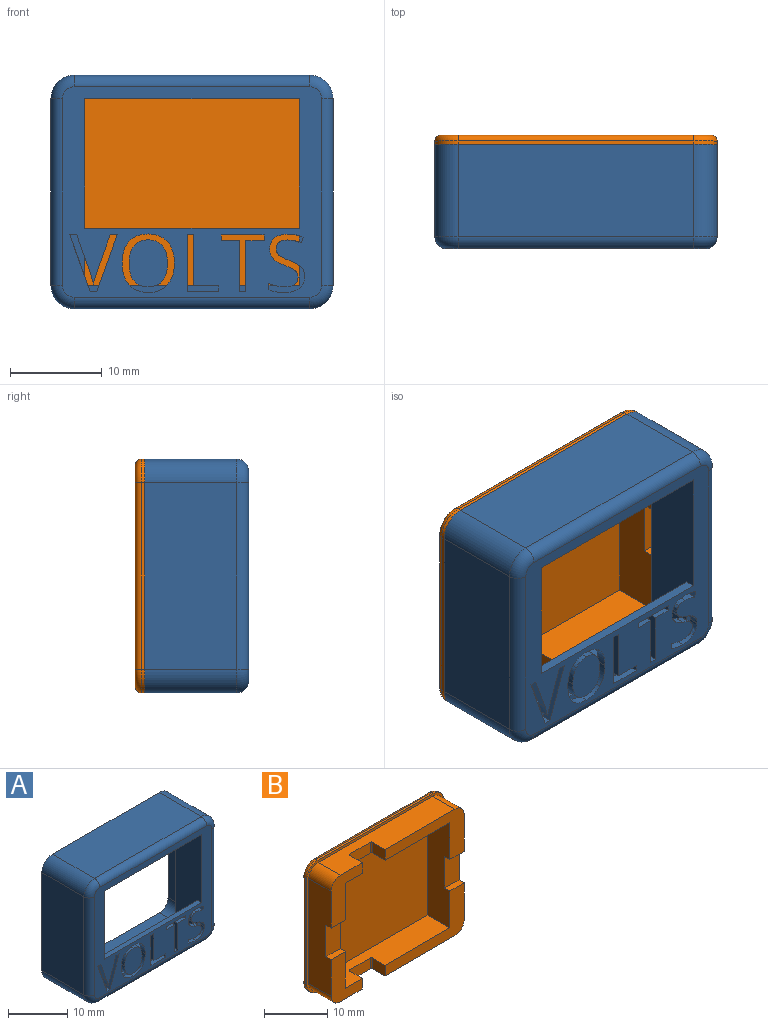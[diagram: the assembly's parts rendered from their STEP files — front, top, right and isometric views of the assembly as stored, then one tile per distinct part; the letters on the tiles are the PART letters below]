
ASSEMBLY  parts=2 mates=1
PART A: 113 faces, bbox 31.1x11.3x25.8 mm
  f0: plane 1.03x0.37mm, normal (0,1,0), area 0.2mm2, adj f7,f18,f90
  f1: plane 23.39x6.23mm, normal (0,1,0), area 91mm2, adj f6,f7,f17,f18,f29,f30,f31,f32
  f2: plane 2.81x2.55mm, normal (0,1,0), area 5.1mm2, adj f17,f64,f65,f66,f67,f68,f69,f70
  f3: plane 4.98x4.17mm, normal (0,1,0), area 17.4mm2, adj f18,f36,f37,f38,f39,f40,f41,f42
  f4: plane 28.13x22.86mm, normal (0,-1,0), area 251.7mm2, adj f6,f7,f8,f17,f29,f30,f31,f32
  f5: plane 29.72x24.92mm, normal (0,1,0), area 250.5mm2, adj f7,f8,f9,f17,f18,f19,f20,f21
  f6: plane 23.37x1.02mm, normal (0,0,1), area 23.7mm2, adj f1,f4,f7,f17
  f7: plane 20.32x6.35mm, normal (1,0,0), area 122.7mm2, adj f0,f1,f4,f5,f6,f8,f18,f99
  f8: plane 23.37x6.35mm, normal (0,0,-1), area 148.4mm2, adj f4,f5,f7,f17
  f9: plane 25.59x10.03mm, normal (0,0,-1), area 241.3mm2, adj f5,f10,f16,f27,f107,f108,f109,f110
  f10: cylinder r=2.54mm len=10.03mm, axis (0,-1,0), area 40mm2, adj f9,f11,f27,f105
  f11: plane 20.32x10.03mm, normal (1,0,0), area 203.9mm2, adj f10,f12,f27,f103
  f12: cylinder r=2.54mm len=10.03mm, axis (0,-1,0), area 40mm2, adj f11,f13,f27,f101
  f13: plane 25.59x10.03mm, normal (0,0,1), area 256.7mm2, adj f12,f14,f27,f100
  f14: cylinder r=2.54mm len=10.03mm, axis (0,-1,0), area 40mm2, adj f13,f15,f27,f102
  f15: plane 20.32x10.03mm, normal (-1,0,0), area 203.9mm2, adj f14,f16,f27,f104
  f16: cylinder r=2.54mm len=10.03mm, axis (0,-1,0), area 40mm2, adj f9,f15,f27,f106
  f17: plane 20.32x6.35mm, normal (-1,0,0), area 122.7mm2, adj f1,f2,f4,f5,f6,f8,f18,f53
  f18: plane 23.37x5.33mm, normal (0,0,1), area 124.6mm2, adj f0,f1,f3,f5,f7,f17,f28,f46
  f19: plane 25.59x4.95mm, normal (0,0,1), area 111.3mm2, adj f5,f20,f26,f27,f108,f109,f110,f111
  f20: cylinder r=2.06mm len=4.95mm, axis (0,-1,0), area 16.1mm2, adj f5,f19,f21,f27
  f21: plane 20.32x4.95mm, normal (1,0,0), area 100.6mm2, adj f5,f20,f22,f27
  f22: cylinder r=2.06mm len=4.95mm, axis (0,-1,0), area 16.1mm2, adj f5,f21,f23,f27
  f23: plane 25.59x4.95mm, normal (0,0,-1), area 126.7mm2, adj f5,f22,f24,f27
  f24: cylinder r=2.06mm len=4.95mm, axis (0,-1,0), area 16.1mm2, adj f5,f23,f25,f27
  f25: plane 20.32x4.95mm, normal (-1,0,0), area 100.6mm2, adj f5,f24,f26,f27
  f26: cylinder r=2.06mm len=4.95mm, axis (0,-1,0), area 16.1mm2, adj f5,f19,f25,f27
  f27: plane 30.67x25.4mm, normal (0,1,0), area 50.6mm2, adj f9,f10,f11,f12,f13,f14,f15,f16
  f28: plane 4.2x0.85mm, normal (0,-1,0), area 2.1mm2, adj f18,f29,f30,f36,f37
  f29: extruded ~2.11x1.02mm, area 2.4mm2, adj f1,f4,f28,f30,f44
  f30: extruded ~2.09x1.02mm, area 2.4mm2, adj f1,f4,f28,f29,f31
  f31: extruded ~2.34x1.02mm, area 2.5mm2, adj f1,f4,f30,f32
  f32: extruded ~2.34x1.02mm, area 2.5mm2, adj f1,f4,f31,f33
  f33: extruded ~2.08x1.02mm, area 2.4mm2, adj f1,f4,f32,f34
  f34: extruded ~2.12x1.02mm, area 2.4mm2, adj f1,f4,f33,f35
  f35: extruded ~2.34x1.02mm, area 2.6mm2, adj f1,f4,f34,f44
  f36: extruded ~1.55x1.02mm, area 1.8mm2, adj f3,f28,f37,f43,f45
  f37: extruded ~1.56x1.02mm, area 1.8mm2, adj f3,f28,f36,f38,f45
  f38: extruded ~1.91x1.02mm, area 2.1mm2, adj f3,f37,f39,f45
  f39: extruded ~1.89x1.02mm, area 2mm2, adj f3,f38,f40,f45
  f40: extruded ~1.56x1.02mm, area 1.8mm2, adj f3,f39,f41,f45
  f41: extruded ~1.55x1.02mm, area 1.8mm2, adj f3,f40,f42,f45
  f42: extruded ~1.89x1.02mm, area 2mm2, adj f3,f41,f43,f45
  f43: extruded ~1.91x1.02mm, area 2.1mm2, adj f3,f36,f42,f45
  f44: extruded ~2.36x1.02mm, area 2.6mm2, adj f1,f4,f29,f35
  f45: plane 5.09x4.17mm, normal (0,-1,0), area 17.6mm2, adj f36,f37,f38,f39,f40,f41,f42,f43
  f46: plane 3.45x0.69mm, normal (0,-1,0), area 2.3mm2, adj f18,f47,f49,f50,f51,f52
  f47: plane 5.54x1.02mm, normal (-1,0,0), area 5.6mm2, adj f1,f4,f46,f48,f52
  f48: plane 1.02x0.72mm, normal (0,0,-1), area 0.7mm2, adj f1,f4,f47,f49
  f49: plane 6.19x1.02mm, normal (1,0,0), area 6.3mm2, adj f1,f4,f46,f48,f50
  f50: plane 3.45x1.02mm, normal (0,0,1), area 3.5mm2, adj f4,f46,f49,f51
  f51: plane 1.02x0.65mm, normal (-1,0,0), area 0.7mm2, adj f4,f46,f50,f52
  f52: plane 2.73x1.02mm, normal (0,0,-1), area 2.8mm2, adj f4,f46,f47,f51
  f53: plane 0.78x0.41mm, normal (0,-1,0), area 0.2mm2, adj f17,f70,f71,f72
  f54: plane 3.89x2.95mm, normal (0,-1,0), area 3mm2, adj f17,f18,f56,f57,f58,f59,f60,f61
  f55: extruded ~1.02x0.76mm, area 0.9mm2, adj f1,f4,f56,f79
  f56: extruded ~1.08x1.02mm, area 1.2mm2, adj f1,f4,f54,f55,f57
  f57: extruded ~1.02x0.89mm, area 0.9mm2, adj f4,f54,f56,f58
  f58: extruded ~1.02x0.83mm, area 0.9mm2, adj f1,f4,f54,f57,f59
  f59: plane 1.02x0.69mm, normal (1,0,0), area 0.7mm2, adj f1,f4,f54,f58,f60
  f60: extruded ~1.69x1.02mm, area 1.8mm2, adj f4,f54,f59,f61
  f61: extruded ~1.61x1.02mm, area 1.7mm2, adj f4,f54,f60,f62
  f62: extruded ~1.27x1.02mm, area 1.5mm2, adj f4,f54,f61,f63
  f63: extruded ~1.03x1.02mm, area 1.1mm2, adj f4,f54,f62,f64
  f64: extruded ~1.34x1.02mm, area 1.6mm2, adj f2,f4,f54,f63,f65
  f65: extruded ~1.02x0.86mm, area 1mm2, adj f2,f4,f64,f66
  f66: extruded ~1.02x0.4mm, area 0.6mm2, adj f2,f4,f65,f67
  f67: extruded ~1.02x0.53mm, area 0.6mm2, adj f2,f4,f66,f68
  f68: extruded ~1.02x0.68mm, area 0.8mm2, adj f2,f4,f67,f69
  f69: extruded ~1.02x0.89mm, area 1mm2, adj f2,f4,f68,f70
  f70: extruded ~1.49x1.02mm, area 1.6mm2, adj f2,f4,f53,f69,f71
  f71: plane 1.02x0.63mm, normal (-0.94,0,0.34), area 0.7mm2, adj f4,f53,f70,f72
  f72: extruded ~1.7x1.02mm, area 1.8mm2, adj f1,f4,f53,f71,f73
  f73: extruded ~1.42x1.02mm, area 1.5mm2, adj f1,f4,f72,f74
  f74: extruded ~1.14x1.02mm, area 1.3mm2, adj f1,f4,f73,f75
  f75: extruded ~1.1x1.02mm, area 1.2mm2, adj f1,f4,f74,f76
  f76: extruded ~1.23x1.02mm, area 1.5mm2, adj f1,f4,f75,f77
  f77: extruded ~1.02x0.92mm, area 1mm2, adj f1,f4,f76,f78
  f78: extruded ~1.02x0.43mm, area 0.6mm2, adj f1,f4,f77,f79
  f79: extruded ~1.02x0.53mm, area 0.6mm2, adj f1,f4,f55,f78
  f80: plane 0.72x0.69mm, normal (0,-1,0), area 0.5mm2, adj f18,f81,f87,f88
  f81: plane 5.55x1.02mm, normal (-1,0,0), area 5.6mm2, adj f1,f4,f80,f82,f88
  f82: plane 1.96x1.02mm, normal (0,0,1), area 2mm2, adj f1,f4,f81,f83
  f83: plane 1.02x0.64mm, normal (-1,0,0), area 0.6mm2, adj f1,f4,f82,f84
  f84: plane 4.64x1.02mm, normal (0,0,-1), area 4.7mm2, adj f1,f4,f83,f85
  f85: plane 1.02x0.64mm, normal (1,0,0), area 0.6mm2, adj f1,f4,f84,f86
  f86: plane 1.96x1.02mm, normal (0,0,1), area 2mm2, adj f1,f4,f85,f87
  f87: plane 5.55x1.02mm, normal (1,0,0), area 5.6mm2, adj f1,f4,f80,f86,f88
  f88: plane 1.02x0.72mm, normal (0,0,1), area 0.7mm2, adj f4,f80,f81,f87
  f89: plane 1.2x0.69mm, normal (0,-1,0), area 0.7mm2, adj f18,f90,f91,f92
  f90: plane 6.19x2.22mm, normal (0.94,0,0.34), area 6.7mm2, adj f0,f4,f89,f91,f98,f99
  f91: plane 1.02x0.71mm, normal (0,0,1), area 0.7mm2, adj f4,f89,f90,f92
  f92: plane 6.19x2.23mm, normal (-0.94,0,0.34), area 6.7mm2, adj f1,f4,f89,f91,f93
  f93: plane 1.02x0.77mm, normal (0,0,-1), area 0.8mm2, adj f1,f4,f92,f94
  f94: plane 3.98x1.41mm, normal (0.94,0,-0.33), area 4.3mm2, adj f1,f4,f93,f95
  f95: extruded ~1.37x1.02mm, area 1.4mm2, adj f1,f4,f94,f96
  f96: extruded ~1.34x1.02mm, area 1.4mm2, adj f1,f4,f95,f97
  f97: plane 4x1.42mm, normal (-0.94,0,-0.33), area 4.3mm2, adj f1,f4,f96,f98,f99
  f98: plane 1.02x0.76mm, normal (0,0,-1), area 0.8mm2, adj f4,f90,f97,f99
  f99: plane 4.47x1.6mm, normal (0,-1,0), area 2.6mm2, adj f7,f90,f97,f98
  f100: cylinder r=1.27mm len=25.59mm, axis (-1,0,0), area 51.1mm2, adj f4,f13,f101,f102
  f101: torus R=1.27mm, axis (0,-1,0), area 6.5mm2, adj f4,f12,f100,f103
  f102: torus R=1.27mm, axis (0,-1,0), area 6.5mm2, adj f4,f14,f100,f104
  f103: cylinder r=1.27mm len=20.32mm, axis (0,0,1), area 40.5mm2, adj f4,f11,f101,f105
  f104: cylinder r=1.27mm len=20.32mm, axis (0,0,-1), area 40.5mm2, adj f4,f15,f102,f106
  f105: torus R=1.27mm, axis (0,-1,0), area 6.5mm2, adj f4,f10,f103,f107
  f106: torus R=1.27mm, axis (0,-1,0), area 6.5mm2, adj f4,f16,f104,f107
  f107: cylinder r=1.27mm len=25.59mm, axis (1,0,0), area 51.1mm2, adj f4,f9,f105,f106
  f108: plane 4.57x0.48mm, normal (0,-1,0), area 2.2mm2, adj f9,f19,f109,f111
  f109: cylinder r=0.25mm len=0.48mm, axis (0,0,-1), area 0.2mm2, adj f9,f19,f108,f110
  f110: plane 2.79x0.48mm, normal (-1,0,0), area 1.3mm2, adj f5,f9,f19,f109
  f111: cylinder r=0.25mm len=0.48mm, axis (0,0,-1), area 0.2mm2, adj f9,f19,f108,f112
  f112: plane 2.79x0.48mm, normal (1,0,0), area 1.3mm2, adj f5,f9,f19,f111
PART B: 51 faces, bbox 31.1x6x25.8 mm
  f0: plane 17.67x9.18mm, normal (0,-1,0), area 58.1mm2, adj f1,f3,f7,f9,f14,f29,f49
  f1: plane 25.59x4.95mm, normal (0,0,-1), area 111.3mm2, adj f0,f10,f11,f14,f17,f46,f47,f48
  f2: plane 25.59x4.95mm, normal (0,0,1), area 111.3mm2, adj f5,f12,f13,f15,f17,f41,f42,f43
  f3: plane 23.37x4.95mm, normal (0,0,1), area 100.3mm2, adj f0,f8,f9,f10,f16,f46,f47,f48
  f4: plane 23.37x4.95mm, normal (0,0,-1), area 100.3mm2, adj f5,f8,f9,f15,f16,f41,f42,f43
  f5: plane 17.67x9.18mm, normal (0,-1,0), area 58.1mm2, adj f2,f4,f7,f9,f13,f28,f41
  f6: plane 20.32x4.95mm, normal (-1,0,0), area 93.7mm2, adj f10,f11,f12,f15,f17,f30,f31,f32
  f7: plane 20.32x4.95mm, normal (1,0,0), area 93.7mm2, adj f0,f5,f13,f14,f17,f27,f28,f29
  f8: plane 20.32x4.95mm, normal (1,0,0), area 93.7mm2, adj f3,f4,f10,f15,f16,f30,f31,f32
  f9: plane 20.32x4.95mm, normal (-1,0,0), area 93.7mm2, adj f0,f3,f4,f5,f16,f27,f28,f29
  f10: plane 9.18x6.97mm, normal (0,-1,0), area 36.1mm2, adj f1,f3,f6,f8,f11,f31,f50
  f11: cylinder r=2.06mm len=4.95mm, axis (0,-1,0), area 16.1mm2, adj f1,f6,f10,f17
  f12: cylinder r=2.06mm len=4.95mm, axis (0,-1,0), area 16.1mm2, adj f2,f6,f15,f17
  f13: cylinder r=2.06mm len=4.95mm, axis (0,-1,0), area 16.1mm2, adj f2,f5,f7,f17
  f14: cylinder r=2.06mm len=4.95mm, axis (0,-1,0), area 16.1mm2, adj f0,f1,f7,f17
  f15: plane 9.18x6.97mm, normal (0,-1,0), area 36.1mm2, adj f2,f4,f6,f8,f12,f32,f44
  f16: plane 23.37x20.32mm, normal (0,-1,0), area 474.8mm2, adj f3,f4,f8,f9
  f17: plane 30.67x25.4mm, normal (0,-1,0), area 50.6mm2, adj f1,f2,f6,f7,f11,f12,f13,f14
  f18: plane 25.59x0.38mm, normal (0,0,-1), area 9.7mm2, adj f17,f19,f25,f38
  f19: cylinder r=2.54mm len=2.54mm, axis (0,-1,0), area 1.5mm2, adj f17,f18,f20,f36
  f20: plane 20.32x0.38mm, normal (-1,0,0), area 7.7mm2, adj f17,f19,f21,f34
  f21: cylinder r=2.54mm len=2.54mm, axis (0,-1,0), area 1.5mm2, adj f17,f20,f22,f33
  f22: plane 25.59x0.38mm, normal (0,0,1), area 9.7mm2, adj f17,f21,f23,f35
  f23: cylinder r=2.54mm len=2.54mm, axis (0,-1,0), area 1.5mm2, adj f17,f22,f24,f37
  f24: plane 20.32x0.38mm, normal (1,0,0), area 7.7mm2, adj f17,f23,f25,f39
  f25: cylinder r=2.54mm len=2.54mm, axis (0,-1,0), area 1.5mm2, adj f17,f18,f24,f40
  f26: plane 29.4x24.13mm, normal (0,1,0), area 706.3mm2, adj f33,f34,f35,f36,f37,f38,f39,f40
  f27: plane 6.1x3.18mm, normal (0,-1,0), area 19.4mm2, adj f7,f9,f28,f29
  f28: plane 3.18x1.14mm, normal (0,0,-1), area 3.6mm2, adj f5,f7,f9,f27
  f29: plane 3.18x1.14mm, normal (0,0,1), area 3.6mm2, adj f0,f7,f9,f27
  f30: plane 6.1x3.18mm, normal (0,-1,0), area 19.4mm2, adj f6,f8,f31,f32
  f31: plane 3.18x1.14mm, normal (0,0,1), area 3.6mm2, adj f6,f8,f10,f30
  f32: plane 3.18x1.14mm, normal (0,0,-1), area 3.6mm2, adj f6,f8,f15,f30
  f33: torus R=1.91mm, axis (0,-1,0), area 3.6mm2, adj f21,f26,f34,f35
  f34: cylinder r=0.64mm len=20.32mm, axis (0,0,1), area 20.3mm2, adj f20,f26,f33,f36
  f35: cylinder r=0.64mm len=25.59mm, axis (1,0,0), area 25.5mm2, adj f22,f26,f33,f37
  f36: torus R=1.91mm, axis (0,-1,0), area 3.6mm2, adj f19,f26,f34,f38
  f37: torus R=1.91mm, axis (0,-1,0), area 3.6mm2, adj f23,f26,f35,f39
  f38: cylinder r=0.64mm len=25.59mm, axis (-1,0,0), area 25.5mm2, adj f18,f26,f36,f40
  f39: cylinder r=0.64mm len=20.32mm, axis (0,0,-1), area 20.3mm2, adj f24,f26,f37,f40
  f40: torus R=1.91mm, axis (0,-1,0), area 3.6mm2, adj f25,f26,f38,f39
  f41: plane 2.79x2.06mm, normal (-1,0,0), area 5.8mm2, adj f2,f4,f5,f42
  f42: cylinder r=0.25mm len=2.06mm, axis (0,0,-1), area 0.8mm2, adj f2,f4,f41,f43
  f43: plane 4.57x2.06mm, normal (0,-1,0), area 9.4mm2, adj f2,f4,f42,f45
  f44: plane 2.79x2.06mm, normal (1,0,0), area 5.8mm2, adj f2,f4,f15,f45
  f45: cylinder r=0.25mm len=2.06mm, axis (0,0,-1), area 0.8mm2, adj f2,f4,f43,f44
  f46: cylinder r=0.25mm len=2.06mm, axis (0,0,-1), area 0.8mm2, adj f1,f3,f47,f50
  f47: plane 4.57x2.06mm, normal (0,-1,0), area 9.4mm2, adj f1,f3,f46,f48
  f48: cylinder r=0.25mm len=2.06mm, axis (0,0,-1), area 0.8mm2, adj f1,f3,f47,f49
  f49: plane 2.79x2.06mm, normal (-1,0,0), area 5.8mm2, adj f0,f1,f3,f48
  f50: plane 2.79x2.06mm, normal (1,0,0), area 5.8mm2, adj f1,f3,f10,f46
PLACE A t=(-20.35,-19.32,-9.56)mm
PLACE B t=(-20.35,-19.32,-9.56)mm
MATE planar A.f13 <-> B.f22  axis (0,0,1) through (-8.6,-8.02,8.22)mm
